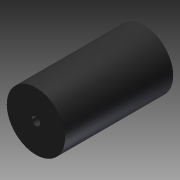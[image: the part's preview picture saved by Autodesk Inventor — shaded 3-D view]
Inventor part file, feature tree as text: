
AUTODESK INVENTOR PART (.ipt)
format: ipt  version: 2012 (Build 160160000, 160)  size: 74,240 bytes
history: native  units: in
note: dims shown in document units (in); Inventor stores cm internally (conversion verified against a paired STEP export)
features: extrude x1, sketch x1
ambient origin geometry x8: Origin, YZ Plane, XZ Plane, XY Plane, X Axis, Y Axis, Z Axis, Center Point
bodies: Solid1 (feature_tree)
feature tree (2):
  extrude  "Extrusion1"  Depth=0.5in
  sketch  "Sketch1"  dims[d0=3.5in d1=0.5in d2=6.5in d3=0.0in]
